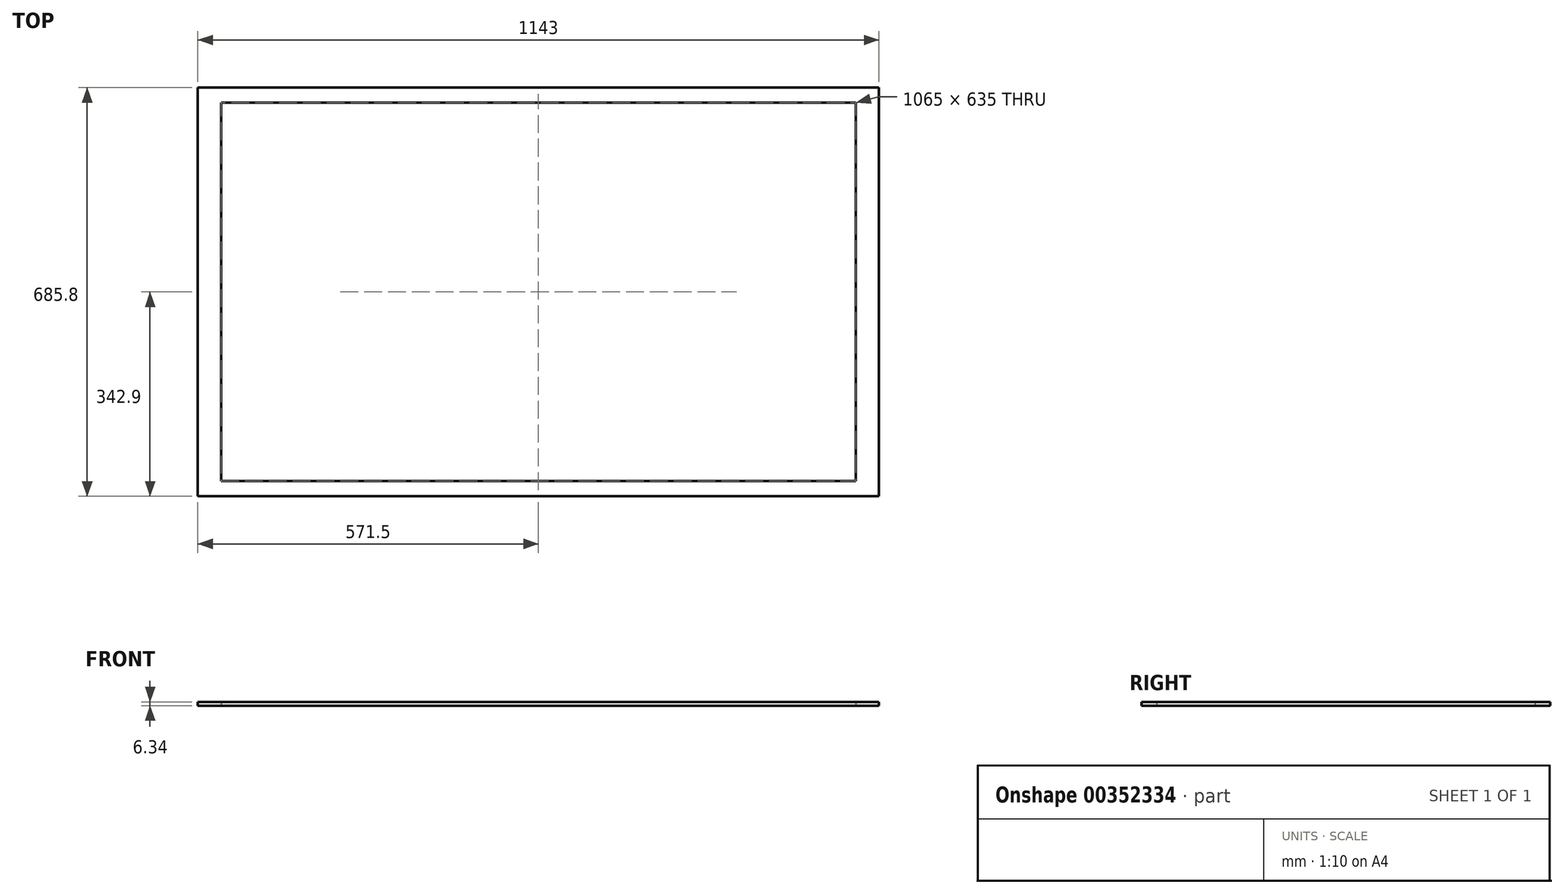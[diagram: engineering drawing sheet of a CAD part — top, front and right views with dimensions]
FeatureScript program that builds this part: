
annotation { "Feature Type Name" : "Feature", "Feature Type Description" : "" }
export const myFeature = defineFeature(function(context is Context, id is Id, definition is map)
    precondition{}
    {
        {
            var Q0;
            Q0=qCreatedBy(makeId("Top.planeOp"),FACE);
            var sketch = newSketch(context, id + "F0", { "sketchPlane" : qUnion([Q0])});
            skPoint(sketch, "E0.middle", {"position": v(0, 0) * mm});
            skLineSegment(sketch, "E1.bottom", {"start": v(-571.5, 342.9) * mm, "end": v(571.5, 342.9) * mm});
            skLineSegment(sketch, "E1.top", {"start": v(-571.5, -342.9) * mm, "end": v(571.5, -342.9) * mm});
            skLineSegment(sketch, "E1.left", {"start": v(-571.5, 342.9) * mm, "end": v(-571.5, -342.9) * mm});
            skLineSegment(sketch, "E1.right", {"start": v(571.5, 342.9) * mm, "end": v(571.5, -342.9) * mm});
            skLineSegment(sketch, "E2.bottom", {"start": v(-532.5, -317.5) * mm, "end": v(532.5, -317.5) * mm});
            skLineSegment(sketch, "E2.top", {"start": v(-532.5, 317.5) * mm, "end": v(532.5, 317.5) * mm});
            skLineSegment(sketch, "E2.left", {"start": v(-532.5, -317.5) * mm, "end": v(-532.5, 317.5) * mm});
            skLineSegment(sketch, "E2.right", {"start": v(532.5, -317.5) * mm, "end": v(532.5, 317.5) * mm});
            skSolve(sketch);
        }
        {
            var Q0;
            Q0=makeQuery(id+"F0.imprint","IMPRINT",FACE,{"disambiguationData":[TD([[makeQuery(id+"F0.imprint","IMPRINT",EDGE,{"derivedFrom":sQuery(id+"F0.wireOp",EDGE,"E1.bottom")}),-1.0]])]});
            extrude(context, id + "F1", {"entities" : qUnion([Q0]), "endBound" : BoundingType.SYMMETRIC, "depth" : 6.35 * mm});
        }
    });
